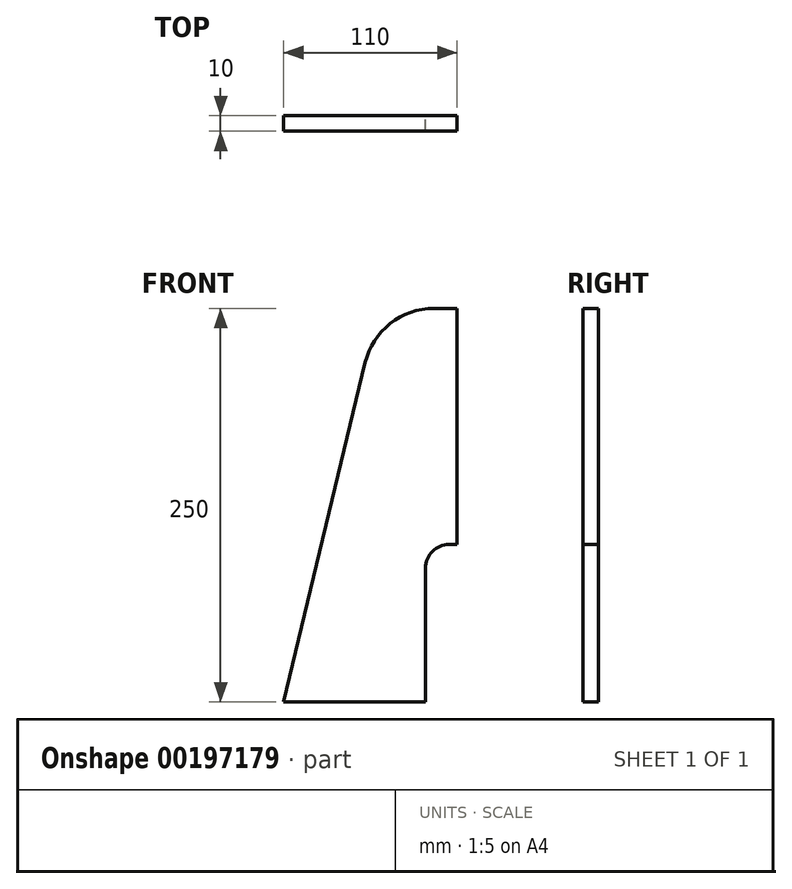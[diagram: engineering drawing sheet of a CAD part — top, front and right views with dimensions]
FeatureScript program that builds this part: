
annotation { "Feature Type Name" : "Feature", "Feature Type Description" : "" }
export const myFeature = defineFeature(function(context is Context, id is Id, definition is map)
    precondition{}
    {
        {
            var Q0;
            Q0=qCreatedBy(makeId("Front.planeOp"),FACE);
            var sketch = newSketch(context, id + "F0", { "sketchPlane" : qUnion([Q0])});
            skLineSegment(sketch, "E0", {"start": v(0, 0) * mm, "end": v(0, 250) * mm, "construction": true});
            skLineSegment(sketch, "E1", {"start": v(0, 250) * mm, "end": v(-14.52, 250) * mm});
            skLineSegment(sketch, "E2", {"start": v(-58.28, 215.5) * mm, "end": v(-110, 0) * mm});
            skLineSegment(sketch, "E3", {"start": v(-110, 0) * mm, "end": v(-20, 0) * mm});
            skLineSegment(sketch, "E4", {"start": v(-20, 0) * mm, "end": v(-20, 85) * mm});
            skLineSegment(sketch, "E5", {"start": v(-5, 100) * mm, "end": v(0, 100) * mm});
            skLineSegment(sketch, "E6", {"start": v(0, 100) * mm, "end": v(0, 250) * mm});
            skPoint(sketch, "E7.visualSharp", {"position": v(-50, 250) * mm});
            skArc(sketch, "E7.filletArc", {"start": v(-14.52, 250) * mm, "mid": v(-42.38, 240.34) * mm, "end": v(-58.28, 215.5) * mm});
            skPoint(sketch, "E8.visualSharp", {"position": v(-20, 100) * mm});
            skArc(sketch, "E8.filletArc", {"start": v(-5, 100) * mm, "mid": v(-15.6, 95.6) * mm, "end": v(-20, 85) * mm});
            skSolve(sketch);
        }
        {
            var Q0;
            Q0 = qSketchRegion(id + "F0", true);
            extrude(context, id + "F1", {"entities" : qUnion([Q0]), "endBound" : BoundingType.SYMMETRIC, "depth" : 10 * mm});
        }
    });
